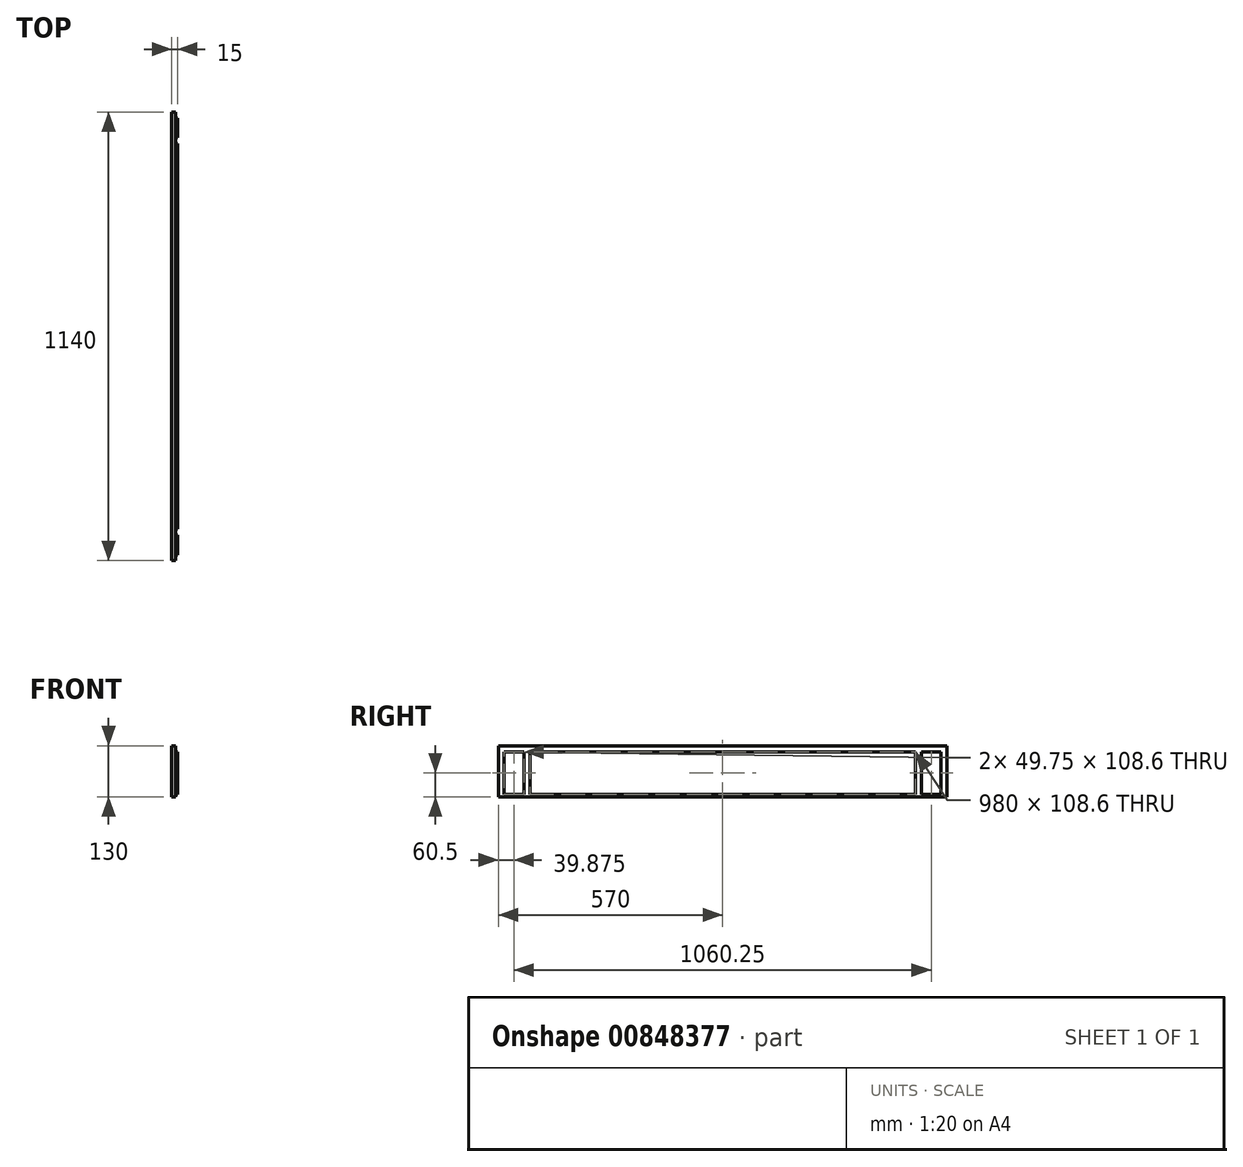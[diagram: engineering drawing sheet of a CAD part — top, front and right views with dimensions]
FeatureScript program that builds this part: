
annotation { "Feature Type Name" : "Feature", "Feature Type Description" : "" }
export const myFeature = defineFeature(function(context is Context, id is Id, definition is map)
    precondition{}
    {
        {
            var Q0;
            Q0=qCreatedBy(makeId("Top.planeOp"),FACE);
            var sketch = newSketch(context, id + "F0", { "sketchPlane" : qUnion([Q0])});
            skLineSegment(sketch, "E0", {"start": v(0, 0) * mm, "end": v(0, -555) * mm});
            skLineSegment(sketch, "E1", {"start": v(0, -555) * mm, "end": v(-5, -555) * mm});
            skLineSegment(sketch, "E2", {"start": v(-5, -555) * mm, "end": v(-5, -570) * mm});
            skLineSegment(sketch, "E3", {"start": v(-5, -570) * mm, "end": v(-15, -570) * mm});
            skLineSegment(sketch, "E4", {"start": v(-15, -570) * mm, "end": v(-15, 0) * mm});
            skLineSegment(sketch, "E5", {"start": v(-15, 0) * mm, "end": v(0, 0) * mm});
            skSolve(sketch);
        }
        {
            var Q0;
            Q0=qSketchRegion(id+"F0",true);
            extrude(context, id + "F1", {"entities" : qUnion([Q0]), "endBound" : BoundingType.SYMMETRIC, "depth" : 130 * mm, "offsetDistance" : 25 * mm});
        }
        {
            var Q0;
            Q0=makeQuery(id+"F1.opExtrude","SWEPT_FACE",FACE,{"disambiguationData":[OSD([sQuery(id+"F0.wireOp",EDGE,"E0")])]});
            var sketch = newSketch(context, id + "F2", { "sketchPlane" : qUnion([Q0])});
            skLineSegment(sketch, "E6", {"start": v(-505.25, -58.8) * mm, "end": v(-505.25, 49.8) * mm});
            skLineSegment(sketch, "E7", {"start": v(-490, 49.8) * mm, "end": v(-490, -58.8) * mm});
            skLineSegment(sketch, "E8", {"start": v(-490, 49.8) * mm, "end": v(0, 49.8) * mm});
            skLineSegment(sketch, "E9", {"start": v(0, 49.8) * mm, "end": v(0, 65) * mm});
            skLineSegment(sketch, "E10", {"start": v(0, 65) * mm, "end": v(-555, 65) * mm});
            skLineSegment(sketch, "E11", {"start": v(-555, 65) * mm, "end": v(-555, 49.8) * mm});
            skLineSegment(sketch, "E12", {"start": v(-555, 49.8) * mm, "end": v(-505.25, 49.8) * mm});
            skLineSegment(sketch, "E13", {"start": v(-505.25, -58.8) * mm, "end": v(-555, -58.8) * mm});
            skLineSegment(sketch, "E14", {"start": v(-555, -58.8) * mm, "end": v(-555, -65) * mm});
            skLineSegment(sketch, "E15", {"start": v(-555, -65) * mm, "end": v(0, -65) * mm});
            skLineSegment(sketch, "E16", {"start": v(0, -65) * mm, "end": v(0, -58.8) * mm});
            skLineSegment(sketch, "E17", {"start": v(0, -58.8) * mm, "end": v(-490, -58.8) * mm});
            skSolve(sketch);
        }
        {
            var Q0;
            Q0=qSketchRegion(id+"F2",true);
            extrude(context, id + "F3", {"entities" : qUnion([Q0]), "operationType" : NewBodyOperationType.REMOVE, "oppositeDirection" : true, "depth" : 5 * mm, "offsetDistance" : 25 * mm});
        }
        {
            var Q0;
            Q0=makeQuery(id+"F1.opExtrude","SWEPT_BODY",BODY,{"disambiguationData":[OSD([sQuery(id+"F0.wireOp",EDGE,"E0"),sQuery(id+"F0.wireOp",EDGE,"E1"),sQuery(id+"F0.wireOp",EDGE,"E2"),sQuery(id+"F0.wireOp",EDGE,"E3"),sQuery(id+"F0.wireOp",EDGE,"E4"),sQuery(id+"F0.wireOp",EDGE,"E5")])]});
            var Q1;
            Q1=makeQuery(id+"F1.opExtrude","SWEPT_FACE",FACE,{"disambiguationData":[OSD([sQuery(id+"F0.wireOp",EDGE,"E5")])]});
            mirror(context, id + "F4", {"operationType" : NewBodyOperationType.ADD, "entities" : qUnion([Q0]), "mirrorPlane" : qUnion([Q1])});
        }
        {
            var Q0;
            Q0=makeQuery(id+"F1.opExtrude","SWEPT_BODY",BODY,{"disambiguationData":[OSD([sQuery(id+"F0.wireOp",EDGE,"E0"),sQuery(id+"F0.wireOp",EDGE,"E1"),sQuery(id+"F0.wireOp",EDGE,"E2"),sQuery(id+"F0.wireOp",EDGE,"E3"),sQuery(id+"F0.wireOp",EDGE,"E4"),sQuery(id+"F0.wireOp",EDGE,"E5")])]});
            transform(context, id + "F5", {"entities" : qUnion([Q0]), "transformType" : TransformType.TRANSLATION_3D, "dx" : 0 * mm, "dy" : 0 * mm, "dz" : 0 * mm, "makeCopy" : true});
        }
        {
            var Q0;
            Q0=qCreatedBy(makeId("Right.planeOp"),FACE);
            cPlane(context, id + "F6", {"entities" : qUnion([Q0]), "cplaneType" : CPlaneType.OFFSET, "offset" : 25 * mm, "width" : 150 * mm, "height" : 150 * mm});
        }
    });
